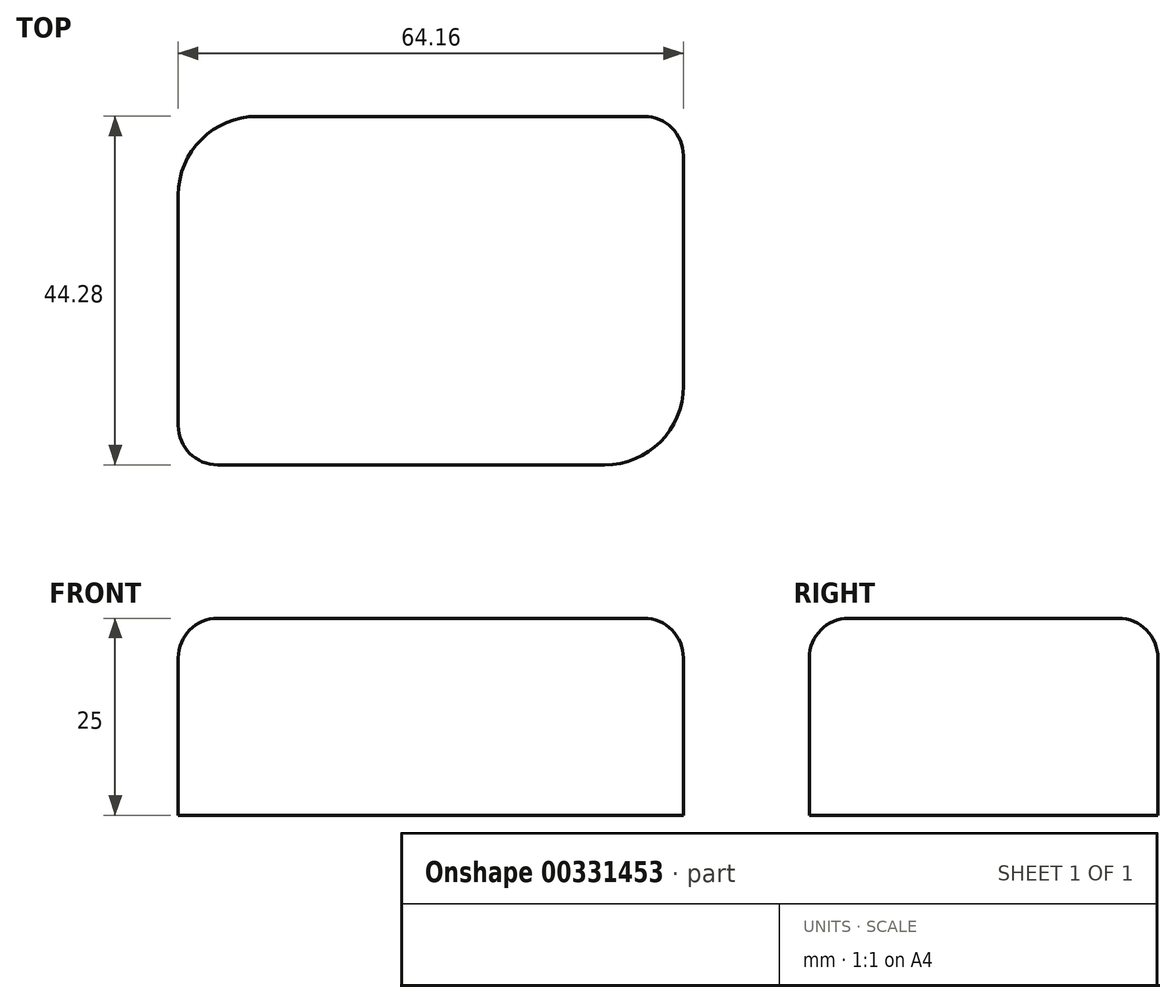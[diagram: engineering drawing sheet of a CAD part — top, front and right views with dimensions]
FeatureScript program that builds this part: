
annotation { "Feature Type Name" : "Feature", "Feature Type Description" : "" }
export const myFeature = defineFeature(function(context is Context, id is Id, definition is map)
    precondition{}
    {
        {
            var Q0;
            Q0=qCreatedBy(makeId("Top.planeOp"),FACE);
            var sketch = newSketch(context, id + "F0", { "sketchPlane" : qUnion([Q0])});
            skLineSegment(sketch, "E0.bottom", {"start": v(-38.6, 25.1) * mm, "end": v(-36.55, 25.1) * mm});
            skLineSegment(sketch, "E0.top", {"start": v(-38.6, 23.69) * mm, "end": v(-36.55, 23.69) * mm});
            skLineSegment(sketch, "E0.left", {"start": v(-38.6, 25.1) * mm, "end": v(-38.6, 23.69) * mm});
            skLineSegment(sketch, "E0.right", {"start": v(-36.55, 25.1) * mm, "end": v(-36.55, 23.69) * mm});
            skLineSegment(sketch, "E1.bottom", {"start": v(-31.57, 23.42) * mm, "end": v(22.59, 23.42) * mm});
            skLineSegment(sketch, "E1.top", {"start": v(-41.57, -20.86) * mm, "end": v(12.59, -20.86) * mm});
            skLineSegment(sketch, "E1.left", {"start": v(-41.57, 13.42) * mm, "end": v(-41.57, -20.86) * mm});
            skLineSegment(sketch, "E1.right", {"start": v(22.59, 23.42) * mm, "end": v(22.59, -10.86) * mm});
            skPoint(sketch, "E2.visualSharp", {"position": v(-41.57, 23.42) * mm});
            skArc(sketch, "E2.filletArc", {"start": v(-31.57, 23.42) * mm, "mid": v(-38.64, 20.49) * mm, "end": v(-41.57, 13.42) * mm});
            skPoint(sketch, "E3.visualSharp", {"position": v(22.59, -20.86) * mm});
            skArc(sketch, "E3.filletArc", {"start": v(12.59, -20.86) * mm, "mid": v(19.66, -17.94) * mm, "end": v(22.59, -10.86) * mm});
            skSolve(sketch);
        }
        {
            var Q0;
            Q0=makeQuery(id+"F0.imprint","IMPRINT",FACE,{"disambiguationData":[TD([[makeQuery(id+"F0.imprint","IMPRINT",EDGE,{"derivedFrom":sQuery(id+"F0.wireOp",EDGE,"E1.bottom")}),-1.0]])]});
            extrude(context, id + "F1", {"entities" : qUnion([Q0]), "depth" : 25 * mm});
        }
        {
            var Q0;
            Q0=makeQuery(id+"F1.opExtrude","SWEPT_EDGE",EDGE,{"disambiguationData":[OSD([sQuery(id+"F0.wireOp",EDGE,"E1.top"),sQuery(id+"F0.wireOp",EDGE,"E1.left")])]});
            var Q1;
            Q1=makeQuery(id+"F1.opExtrude","CAP_EDGE",EDGE,{"disambiguationData":[OSD([sQuery(id+"F0.wireOp",EDGE,"E1.left")])],"isStart":false});
            var Q2;
            Q2=makeQuery(id+"F1.opExtrude","CAP_EDGE",EDGE,{"disambiguationData":[OSD([sQuery(id+"F0.wireOp",EDGE,"E1.top")])],"isStart":false});
            fillet(context, id + "F2", {"entities" : qUnion([Q0, Q1, Q2]), "radius" : 5 * mm, "tangentPropagation" : true, "allowEdgeOverflow" : false});
        }
        {
            var Q0;
            Q0=makeQuery(id+"F1.opExtrude","SWEPT_EDGE",EDGE,{"disambiguationData":[OSD([sQuery(id+"F0.wireOp",EDGE,"E1.bottom"),sQuery(id+"F0.wireOp",EDGE,"E1.right")])]});
            fillet(context, id + "F3", {"entities" : qUnion([Q0]), "radius" : 5 * mm, "tangentPropagation" : true, "allowEdgeOverflow" : false});
        }
    });
